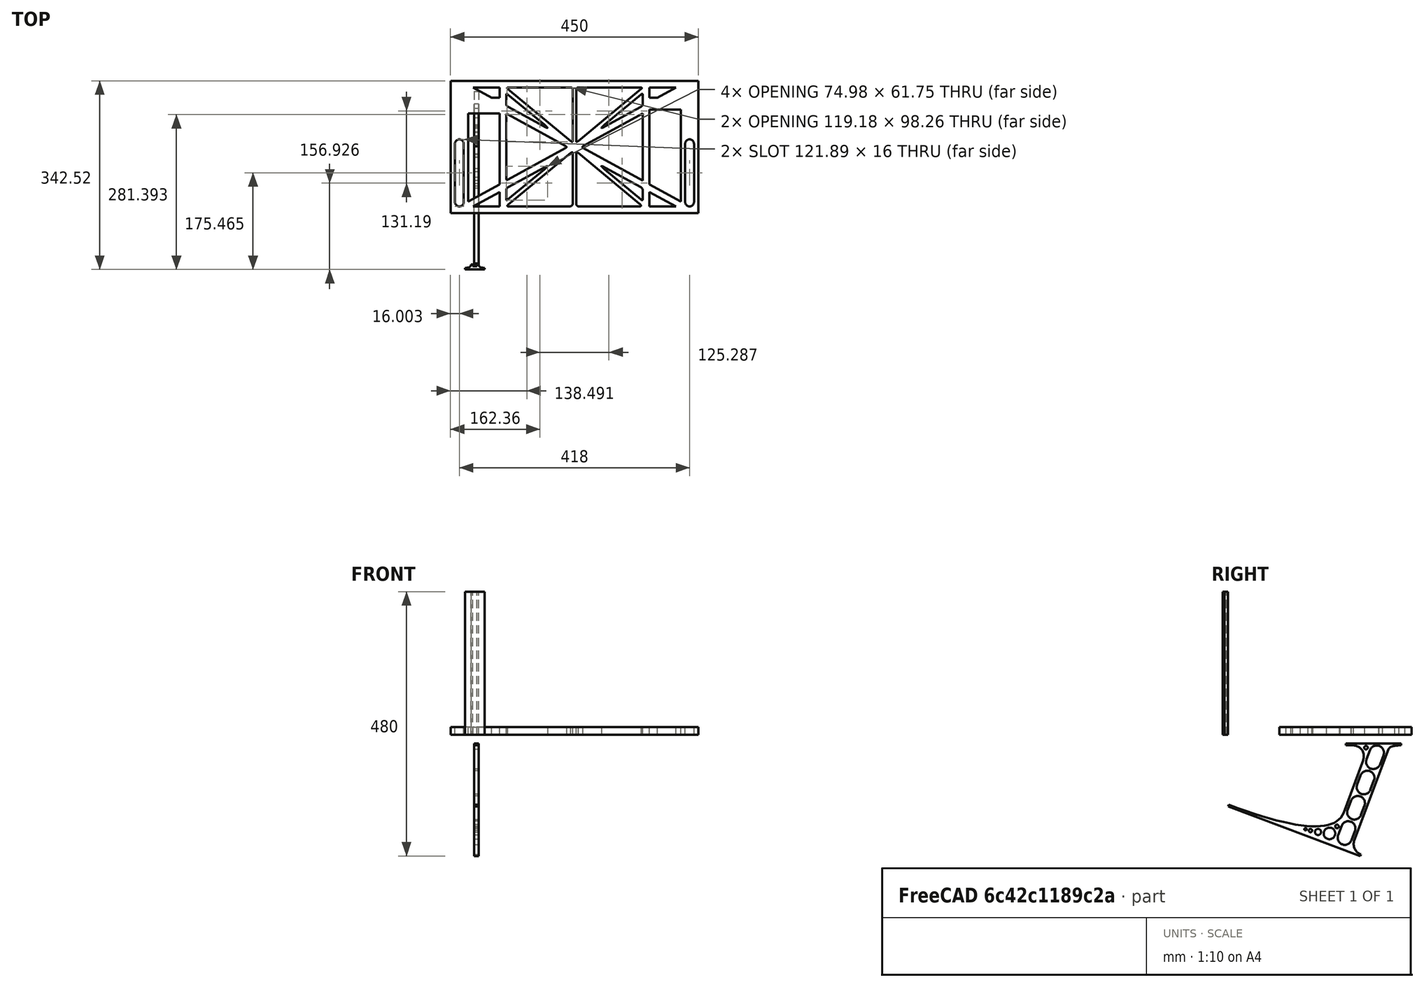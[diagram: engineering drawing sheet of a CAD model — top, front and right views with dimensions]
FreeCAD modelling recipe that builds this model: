
FCSTD DOCUMENT  (FreeCAD 0.19R0.19.2)
Label: laptopStand088
License: All rights reserved
LicenseURL: http://en.wikipedia.org/wiki/All_rights_reserved
objects: Sketcher::SketchObject×3, Part::Extrusion×3
note: 6 computed .brp shape members not serialized (recipe doc carries the construction recipe); baked Part::Feature solids carry a one-line shape summary decoded from their .brp

FEATURE [Sketcher::SketchObject] Sketch
  FullyConstrained = true
  sketch-geometry (232):
    g0: LineSegment StartX=-10.9272 StartY=-82.7794 StartZ=0 EndX=46.0728 EndY=-51.4823 EndZ=0
    g1: LineSegment StartX=366.073 StartY=-91.7794 StartZ=0 EndX=318.073 EndY=-65.424 EndZ=0
    g2: LineSegment StartX=-10.9272 StartY=77.3346 StartZ=0 EndX=-10.9272 EndY=-82.7794 EndZ=0
    g3: LineSegment StartX=375.073 StartY=-82.7794 StartZ=0 EndX=375.073 EndY=83.9235 EndZ=0
    g4: LineSegment StartX=-1.92719 StartY=-91.7794 StartZ=0 EndX=46.0728 EndY=-91.7794 EndZ=0
    g5: LineSegment StartX=318.073 StartY=124.221 StartZ=0 EndX=366.073 EndY=124.221 EndZ=0
    g6: LineSegment StartX=306.073 StartY=77.3346 StartZ=0 EndX=306.073 EndY=-44.8935 EndZ=0
    g7: LineSegment StartX=318.073 StartY=83.9235 StartZ=0 EndX=318.073 EndY=-51.4823 EndZ=0
    g8: LineSegment StartX=318.073 StartY=-51.4823 StartZ=0 EndX=375.073 EndY=-82.7794 EndZ=0
    g9: LineSegment StartX=318.073 StartY=-65.424 StartZ=0 EndX=318.073 EndY=-91.7794 EndZ=0
    g10: LineSegment StartX=318.073 StartY=-91.7794 StartZ=0 EndX=366.073 EndY=-91.7794 EndZ=0
    g11: LineSegment StartX=46.0728 StartY=-65.424 StartZ=0 EndX=-1.92719 EndY=-91.7794 EndZ=0
    g12: LineSegment StartX=46.0728 StartY=-65.424 StartZ=0 EndX=46.0728 EndY=-91.7794 EndZ=0
    g13: LineSegment StartX=46.0728 StartY=77.3346 StartZ=0 EndX=46.0728 EndY=-51.4823 EndZ=0
    g14: LineSegment StartX=-42.9272 StartY=136.221 StartZ=0 EndX=-42.9272 EndY=-103.779 EndZ=0
    g15: LineSegment StartX=407.073 StartY=136.221 StartZ=0 EndX=407.073 EndY=-103.779 EndZ=0
    g16: ArcOfCircle CenterX=-26.9272 CenterY=22.1087 CenterZ=0 NormalX=0 NormalY=0 NormalZ=1 AngleXU=0 Radius=8 StartAngle=1e-16 EndAngle=3.14159
    g17: ArcOfCircle CenterX=-26.9272 CenterY=-83.7794 CenterZ=0 NormalX=0 NormalY=0 NormalZ=1 AngleXU=0 Radius=8 StartAngle=3.14159 EndAngle=6.28319
    g18: LineSegment StartX=-34.9272 StartY=22.1087 StartZ=0 EndX=-34.9272 EndY=-83.7794 EndZ=0
    g19: LineSegment StartX=-18.9272 StartY=22.1087 StartZ=0 EndX=-18.9272 EndY=-83.7794 EndZ=0
    g20: ArcOfCircle CenterX=391.073 CenterY=22.1087 CenterZ=0 NormalX=0 NormalY=0 NormalZ=1 AngleXU=0 Radius=8 StartAngle=-4.4e-15 EndAngle=3.14159
    g21: LineSegment StartX=399.073 StartY=22.1087 StartZ=0 EndX=399.073 EndY=-83.7794 EndZ=0
    g22: LineSegment StartX=383.073 StartY=22.1087 StartZ=0 EndX=383.073 EndY=-83.7794 EndZ=0
    g23: ArcOfCircle CenterX=391.073 CenterY=-83.7794 CenterZ=0 NormalX=0 NormalY=0 NormalZ=1 AngleXU=0 Radius=8 StartAngle=3.14159 EndAngle=6.28319
    g24: Circle CenterX=175.022 CenterY=27.0628 CenterZ=0 NormalX=0 NormalY=0 NormalZ=1 AngleXU=0 Radius=1
    g25: Circle CenterX=179.022 CenterY=24.8665 CenterZ=0 NormalX=0 NormalY=0 NormalZ=1 AngleXU=0 Radius=1
    g26: Circle CenterX=179.022 CenterY=27.0628 CenterZ=0 NormalX=0 NormalY=0 NormalZ=1 AngleXU=0 Radius=1
    g27: BSplineCurve PolesCount=3 KnotsCount=2 Degree=2 IsPeriodic=0
    g28: GeomPoint X=175.022 Y=27.0628 Z=0
    g29: GeomPoint X=179.022 Y=27.0628 Z=0
    g30: Circle CenterX=189.124 CenterY=27.0628 CenterZ=0 NormalX=0 NormalY=0 NormalZ=1 AngleXU=0 Radius=1
    g31: Circle CenterX=185.124 CenterY=24.8665 CenterZ=0 NormalX=0 NormalY=0 NormalZ=1 AngleXU=0 Radius=1
    g32: Circle CenterX=185.124 CenterY=27.0628 CenterZ=0 NormalX=0 NormalY=0 NormalZ=1 AngleXU=0 Radius=1
    g33: BSplineCurve PolesCount=3 KnotsCount=2 Degree=2 IsPeriodic=0
    g34: GeomPoint X=189.124 Y=27.0628 Z=0
    g35: GeomPoint X=185.124 Y=27.0628 Z=0
    g36: Circle CenterX=175.022 CenterY=5.37834 CenterZ=0 NormalX=0 NormalY=0 NormalZ=1 AngleXU=0 Radius=1
    g37: Circle CenterX=179.022 CenterY=7.57463 CenterZ=0 NormalX=0 NormalY=0 NormalZ=1 AngleXU=0 Radius=1
    g38: Circle CenterX=179.022 CenterY=5.34704 CenterZ=0 NormalX=0 NormalY=0 NormalZ=1 AngleXU=0 Radius=1
    g39: BSplineCurve PolesCount=3 KnotsCount=2 Degree=2 IsPeriodic=0
    g40: GeomPoint X=175.022 Y=5.37834 Z=0
    g41: GeomPoint X=179.022 Y=5.34704 Z=0
    g42: Circle CenterX=189.124 CenterY=5.37834 CenterZ=0 NormalX=0 NormalY=0 NormalZ=1 AngleXU=0 Radius=1
    g43: Circle CenterX=185.124 CenterY=7.57463 CenterZ=0 NormalX=0 NormalY=0 NormalZ=1 AngleXU=0 Radius=1
    g44: Circle CenterX=185.124 CenterY=5.34704 CenterZ=0 NormalX=0 NormalY=0 NormalZ=1 AngleXU=0 Radius=1
    g45: BSplineCurve PolesCount=3 KnotsCount=2 Degree=2 IsPeriodic=0
    g46: GeomPoint X=189.124 Y=5.37834 Z=0
    g47: GeomPoint X=185.124 Y=5.34704 Z=0
    g48: Circle CenterX=165.871 CenterY=18.1458 CenterZ=0 NormalX=0 NormalY=0 NormalZ=1 AngleXU=0 Radius=1
    g49: Circle CenterX=169.377 CenterY=16.2206 CenterZ=0 NormalX=0 NormalY=0 NormalZ=1 AngleXU=0 Radius=1
    g50: Circle CenterX=165.871 CenterY=14.2954 CenterZ=0 NormalX=0 NormalY=0 NormalZ=1 AngleXU=0 Radius=1
    g51: BSplineCurve PolesCount=3 KnotsCount=2 Degree=2 IsPeriodic=0
    g52: GeomPoint X=165.871 Y=18.1458 Z=0
    g53: GeomPoint X=165.871 Y=14.2954 Z=0
    g54: Circle CenterX=198.275 CenterY=18.1458 CenterZ=0 NormalX=0 NormalY=0 NormalZ=1 AngleXU=0 Radius=1
    g55: Circle CenterX=194.768 CenterY=16.2206 CenterZ=0 NormalX=0 NormalY=0 NormalZ=1 AngleXU=0 Radius=1
    g56: Circle CenterX=198.275 CenterY=14.2954 CenterZ=0 NormalX=0 NormalY=0 NormalZ=1 AngleXU=0 Radius=1
    g57: BSplineCurve PolesCount=3 KnotsCount=2 Degree=2 IsPeriodic=0
    g58: GeomPoint X=198.275 Y=18.1458 Z=0
    g59: GeomPoint X=198.275 Y=14.2954 Z=0
    g60: LineSegment StartX=198.275 StartY=18.1458 StartZ=0 EndX=306.073 EndY=77.3346 EndZ=0
    g61: LineSegment StartX=198.275 StartY=14.2954 StartZ=0 EndX=306.073 EndY=-44.8935 EndZ=0
    g62: LineSegment StartX=407.073 StartY=-103.779 StartZ=0 EndX=-42.9272 EndY=-103.779 EndZ=0
    g63: LineSegment StartX=407.073 StartY=136.221 StartZ=0 EndX=-42.9272 EndY=136.221 EndZ=0
    g64: LineSegment StartX=46.0728 StartY=77.3346 StartZ=0 EndX=-10.9272 EndY=77.3346 EndZ=0
    g65: LineSegment StartX=46.0728 StartY=105.865 StartZ=0 EndX=31.5028 EndY=105.865 EndZ=0
    g66: LineSegment StartX=46.0728 StartY=124.221 StartZ=0 EndX=46.0728 EndY=105.865 EndZ=0
    g67: LineSegment StartX=-1.92719 StartY=124.221 StartZ=0 EndX=31.5028 EndY=105.865 EndZ=0
    g68: LineSegment StartX=46.0728 StartY=124.221 StartZ=0 EndX=-1.92719 EndY=124.221 EndZ=0
    g69: LineSegment StartX=318.073 StartY=83.9235 StartZ=0 EndX=375.073 EndY=83.9235 EndZ=0
    g70: LineSegment StartX=318.073 StartY=105.865 StartZ=0 EndX=332.643 EndY=105.865 EndZ=0
    g71: LineSegment StartX=332.643 StartY=105.865 StartZ=0 EndX=366.073 EndY=124.221 EndZ=0
    g72: LineSegment StartX=318.073 StartY=124.221 StartZ=0 EndX=318.073 EndY=105.865 EndZ=0
    g73: Circle CenterX=125.607 CenterY=54.1951 CenterZ=0 NormalX=0 NormalY=0 NormalZ=1 AngleXU=0 Radius=1
    g74: Circle CenterX=139.632 CenterY=46.4944 CenterZ=0 NormalX=0 NormalY=0 NormalZ=1 AngleXU=0 Radius=1
    g75: Circle CenterX=127.326 CenterY=56.7187 CenterZ=0 NormalX=0 NormalY=0 NormalZ=1 AngleXU=0 Radius=1
    g76: BSplineCurve PolesCount=3 KnotsCount=2 Degree=2 IsPeriodic=0
    g77: GeomPoint X=125.607 Y=54.1951 Z=0
    g78: GeomPoint X=127.326 Y=56.7187 Z=0
    g79: Circle CenterX=236.821 CenterY=56.7187 CenterZ=0 NormalX=0 NormalY=0 NormalZ=1 AngleXU=0 Radius=1
    g80: Circle CenterX=224.513 CenterY=46.4944 CenterZ=0 NormalX=0 NormalY=0 NormalZ=1 AngleXU=0 Radius=1
    g81: Circle CenterX=238.538 CenterY=54.1951 CenterZ=0 NormalX=0 NormalY=0 NormalZ=1 AngleXU=0 Radius=1
    g82: BSplineCurve PolesCount=3 KnotsCount=2 Degree=2 IsPeriodic=0
    g83: GeomPoint X=236.821 Y=56.7187 Z=0
    g84: GeomPoint X=238.538 Y=54.1951 Z=0
    g85: Circle CenterX=238.538 CenterY=-21.7539 CenterZ=0 NormalX=0 NormalY=0 NormalZ=1 AngleXU=0 Radius=1
    g86: Circle CenterX=224.513 CenterY=-14.0532 CenterZ=0 NormalX=0 NormalY=0 NormalZ=1 AngleXU=0 Radius=1
    g87: Circle CenterX=236.821 CenterY=-24.2775 CenterZ=0 NormalX=0 NormalY=0 NormalZ=1 AngleXU=0 Radius=1
    g88: BSplineCurve PolesCount=3 KnotsCount=2 Degree=2 IsPeriodic=0
    g89: GeomPoint X=238.538 Y=-21.7539 Z=0
    g90: GeomPoint X=236.821 Y=-24.2775 Z=0
    g91: Circle CenterX=125.607 CenterY=-21.7539 CenterZ=0 NormalX=0 NormalY=0 NormalZ=1 AngleXU=0 Radius=1
    g92: Circle CenterX=139.632 CenterY=-14.0532 CenterZ=0 NormalX=0 NormalY=0 NormalZ=1 AngleXU=0 Radius=1
    g93: Circle CenterX=127.325 CenterY=-24.2775 CenterZ=0 NormalX=0 NormalY=0 NormalZ=1 AngleXU=0 Radius=1
    g94: BSplineCurve PolesCount=3 KnotsCount=2 Degree=2 IsPeriodic=0
    g95: GeomPoint X=125.607 Y=-21.7539 Z=0
    g96: GeomPoint X=127.325 Y=-24.2775 Z=0
    g97: Circle CenterX=302.996 CenterY=111.695 CenterZ=0 NormalX=0 NormalY=0 NormalZ=1 AngleXU=0 Radius=1
    g98: Circle CenterX=306.073 CenterY=114.251 CenterZ=0 NormalX=0 NormalY=0 NormalZ=1 AngleXU=0 Radius=1
    g99: Circle CenterX=306.073 CenterY=110.251 CenterZ=0 NormalX=0 NormalY=0 NormalZ=1 AngleXU=0 Radius=1
    g100: BSplineCurve PolesCount=3 KnotsCount=2 Degree=2 IsPeriodic=0
    g101: GeomPoint X=302.996 Y=111.695 Z=0
    g102: GeomPoint X=306.073 Y=110.251 Z=0
    g103: Circle CenterX=306.073 CenterY=95.2763 CenterZ=0 NormalX=0 NormalY=0 NormalZ=1 AngleXU=0 Radius=1
    g104: Circle CenterX=306.073 CenterY=91.2763 CenterZ=0 NormalX=0 NormalY=0 NormalZ=1 AngleXU=0 Radius=1
    g105: Circle CenterX=302.567 CenterY=89.3511 CenterZ=0 NormalX=0 NormalY=0 NormalZ=1 AngleXU=0 Radius=1
    g106: BSplineCurve PolesCount=3 KnotsCount=2 Degree=2 IsPeriodic=0
    g107: GeomPoint X=306.073 Y=95.2763 Z=0
    g108: GeomPoint X=302.567 Y=89.3511 Z=0
    g109: LineSegment StartX=306.073 StartY=110.251 StartZ=0 EndX=306.073 EndY=95.2763 EndZ=0
    g110: LineSegment StartX=302.996 StartY=111.695 StartZ=0 EndX=236.821 EndY=56.7187 EndZ=0
    g111: LineSegment StartX=238.538 StartY=54.1951 StartZ=0 EndX=302.567 EndY=89.3511 EndZ=0
    g112: Circle CenterX=61.1496 CenterY=111.695 CenterZ=0 NormalX=0 NormalY=0 NormalZ=1 AngleXU=0 Radius=1
    g113: Circle CenterX=58.0728 CenterY=114.251 CenterZ=0 NormalX=0 NormalY=0 NormalZ=1 AngleXU=0 Radius=1
    g114: Circle CenterX=58.0728 CenterY=110.251 CenterZ=0 NormalX=0 NormalY=0 NormalZ=1 AngleXU=0 Radius=1
    g115: BSplineCurve PolesCount=3 KnotsCount=2 Degree=2 IsPeriodic=0
    g116: GeomPoint X=61.1496 Y=111.695 Z=0
    g117: GeomPoint X=58.0728 Y=110.251 Z=0
    g118: Circle CenterX=61.5791 CenterY=89.3511 CenterZ=0 NormalX=0 NormalY=0 NormalZ=1 AngleXU=0 Radius=1
    g119: Circle CenterX=58.0728 CenterY=91.2763 CenterZ=0 NormalX=0 NormalY=0 NormalZ=1 AngleXU=0 Radius=1
    g120: Circle CenterX=58.0728 CenterY=95.2763 CenterZ=0 NormalX=0 NormalY=0 NormalZ=1 AngleXU=0 Radius=1
    g121: BSplineCurve PolesCount=3 KnotsCount=2 Degree=2 IsPeriodic=0
    g122: GeomPoint X=61.5791 Y=89.3511 Z=0
    g123: GeomPoint X=58.0728 Y=95.2763 Z=0
    g124: LineSegment StartX=58.0728 StartY=110.251 StartZ=0 EndX=58.0728 EndY=95.2763 EndZ=0
    g125: LineSegment StartX=61.1496 StartY=111.695 StartZ=0 EndX=127.326 EndY=56.7187 EndZ=0
    g126: LineSegment StartX=125.607 StartY=54.1951 StartZ=0 EndX=61.5791 EndY=89.3511 EndZ=0
    g127: Circle CenterX=61.5791 CenterY=-56.9099 CenterZ=0 NormalX=0 NormalY=0 NormalZ=1 AngleXU=0 Radius=1
    g128: Circle CenterX=58.0728 CenterY=-58.8351 CenterZ=0 NormalX=0 NormalY=0 NormalZ=1 AngleXU=0 Radius=1
    g129: Circle CenterX=58.0728 CenterY=-62.8351 CenterZ=0 NormalX=0 NormalY=0 NormalZ=1 AngleXU=0 Radius=1
    g130: BSplineCurve PolesCount=3 KnotsCount=2 Degree=2 IsPeriodic=0
    g131: GeomPoint X=61.5791 Y=-56.9099 Z=0
    g132: GeomPoint X=58.0728 Y=-62.8351 Z=0
    g133: Circle CenterX=58.0728 CenterY=-77.8102 CenterZ=0 NormalX=0 NormalY=0 NormalZ=1 AngleXU=0 Radius=1
    g134: Circle CenterX=58.0728 CenterY=-81.8102 CenterZ=0 NormalX=0 NormalY=0 NormalZ=1 AngleXU=0 Radius=1
    g135: Circle CenterX=61.1496 CenterY=-79.2541 CenterZ=0 NormalX=0 NormalY=0 NormalZ=1 AngleXU=0 Radius=1
    g136: BSplineCurve PolesCount=3 KnotsCount=2 Degree=2 IsPeriodic=0
    g137: GeomPoint X=58.0728 Y=-77.8102 Z=0
    g138: GeomPoint X=61.1496 Y=-79.2541 Z=0
    g139: LineSegment StartX=58.0728 StartY=-62.8351 StartZ=0 EndX=58.0728 EndY=-77.8102 EndZ=0
    g140: LineSegment StartX=61.1496 StartY=-79.2541 StartZ=0 EndX=127.325 EndY=-24.2775 EndZ=0
    g141: LineSegment StartX=125.607 StartY=-21.7539 StartZ=0 EndX=61.5791 EndY=-56.9099 EndZ=0
    g142: Circle CenterX=302.567 CenterY=-56.9099 CenterZ=0 NormalX=0 NormalY=0 NormalZ=1 AngleXU=0 Radius=1
    g143: Circle CenterX=306.073 CenterY=-58.8351 CenterZ=0 NormalX=0 NormalY=0 NormalZ=1 AngleXU=0 Radius=1
    g144: Circle CenterX=306.073 CenterY=-62.8351 CenterZ=0 NormalX=0 NormalY=0 NormalZ=1 AngleXU=0 Radius=1
    g145: BSplineCurve PolesCount=3 KnotsCount=2 Degree=2 IsPeriodic=0
    g146: GeomPoint X=302.567 Y=-56.9099 Z=0
    g147: GeomPoint X=306.073 Y=-62.8351 Z=0
    g148: Circle CenterX=302.996 CenterY=-79.2541 CenterZ=0 NormalX=0 NormalY=0 NormalZ=1 AngleXU=0 Radius=1
    g149: Circle CenterX=306.073 CenterY=-81.8102 CenterZ=0 NormalX=0 NormalY=0 NormalZ=1 AngleXU=0 Radius=1
    g150: Circle CenterX=306.073 CenterY=-77.8102 CenterZ=0 NormalX=0 NormalY=0 NormalZ=1 AngleXU=0 Radius=1
    g151: BSplineCurve PolesCount=3 KnotsCount=2 Degree=2 IsPeriodic=0
    g152: GeomPoint X=302.996 Y=-79.2541 Z=0
    g153: GeomPoint X=306.073 Y=-77.8102 Z=0
    g154: LineSegment StartX=306.073 StartY=-62.8351 StartZ=0 EndX=306.073 EndY=-77.8102 EndZ=0
    g155: LineSegment StartX=302.996 StartY=-79.2541 StartZ=0 EndX=236.821 EndY=-24.2775 EndZ=0
    g156: LineSegment StartX=238.538 StartY=-21.7539 StartZ=0 EndX=302.567 EndY=-56.9099 EndZ=0
    g157: Circle CenterX=61.6457 CenterY=-88.8112 CenterZ=0 NormalX=0 NormalY=0 NormalZ=1 AngleXU=0 Radius=1
    g158: Circle CenterX=58.0728 CenterY=-91.7794 CenterZ=0 NormalX=0 NormalY=0 NormalZ=1 AngleXU=0 Radius=1
    g159: Circle CenterX=63.9135 CenterY=-91.7794 CenterZ=0 NormalX=0 NormalY=0 NormalZ=1 AngleXU=0 Radius=1
    g160: BSplineCurve PolesCount=3 KnotsCount=2 Degree=2 IsPeriodic=0
    g161: GeomPoint X=61.6457 Y=-88.8112 Z=0
    g162: GeomPoint X=63.9135 Y=-91.7794 Z=0
    g163: Circle CenterX=179.022 CenterY=-85.8163 CenterZ=0 NormalX=0 NormalY=0 NormalZ=1 AngleXU=0 Radius=1
    g164: Circle CenterX=179.022 CenterY=-91.7794 CenterZ=0 NormalX=0 NormalY=0 NormalZ=1 AngleXU=0 Radius=1
    g165: Circle CenterX=171.895 CenterY=-91.7794 CenterZ=0 NormalX=0 NormalY=0 NormalZ=1 AngleXU=0 Radius=1
    g166: BSplineCurve PolesCount=3 KnotsCount=2 Degree=2 IsPeriodic=0
    g167: GeomPoint X=179.022 Y=-85.8163 Z=0
    g168: GeomPoint X=171.895 Y=-91.7794 Z=0
    g169: Circle CenterX=185.124 CenterY=-86.2028 CenterZ=0 NormalX=0 NormalY=0 NormalZ=1 AngleXU=0 Radius=1
    g170: Circle CenterX=185.124 CenterY=-91.7794 CenterZ=0 NormalX=0 NormalY=0 NormalZ=1 AngleXU=0 Radius=1
    g171: Circle CenterX=191.747 CenterY=-91.7794 CenterZ=0 NormalX=0 NormalY=0 NormalZ=1 AngleXU=0 Radius=1
    g172: BSplineCurve PolesCount=3 KnotsCount=2 Degree=2 IsPeriodic=0
    g173: GeomPoint X=185.124 Y=-86.2028 Z=0
    g174: GeomPoint X=191.747 Y=-91.7794 Z=0
    g175: Circle CenterX=299.888 CenterY=-86.6413 CenterZ=0 NormalX=0 NormalY=0 NormalZ=1 AngleXU=0 Radius=1
    g176: Circle CenterX=306.073 CenterY=-91.7794 CenterZ=0 NormalX=0 NormalY=0 NormalZ=1 AngleXU=0 Radius=1
    g177: Circle CenterX=298.776 CenterY=-91.7794 CenterZ=0 NormalX=0 NormalY=0 NormalZ=1 AngleXU=0 Radius=1
    g178: BSplineCurve PolesCount=3 KnotsCount=2 Degree=2 IsPeriodic=0
    g179: GeomPoint X=299.888 Y=-86.6413 Z=0
    g180: GeomPoint X=298.776 Y=-91.7794 Z=0
    g181: LineSegment StartX=189.124 StartY=5.37834 StartZ=0 EndX=299.888 EndY=-86.6413 EndZ=0
    g182: LineSegment StartX=298.776 StartY=-91.7794 StartZ=0 EndX=191.747 EndY=-91.7794 EndZ=0
    g183: LineSegment StartX=185.124 StartY=-86.2028 StartZ=0 EndX=185.124 EndY=5.34704 EndZ=0
    g184: LineSegment StartX=179.022 StartY=5.34704 StartZ=0 EndX=179.022 EndY=-85.8163 EndZ=0
    g185: LineSegment StartX=171.895 StartY=-91.7794 StartZ=0 EndX=63.9135 EndY=-91.7794 EndZ=0
    g186: LineSegment StartX=61.6457 StartY=-88.8112 StartZ=0 EndX=175.022 EndY=5.37834 EndZ=0
    g187: Circle CenterX=302.073 CenterY=124.221 CenterZ=0 NormalX=0 NormalY=0 NormalZ=1 AngleXU=0 Radius=1
    g188: Circle CenterX=306.073 CenterY=124.221 CenterZ=0 NormalX=0 NormalY=0 NormalZ=1 AngleXU=0 Radius=1
    g189: Circle CenterX=302.996 CenterY=121.665 CenterZ=0 NormalX=0 NormalY=0 NormalZ=1 AngleXU=0 Radius=1
    g190: BSplineCurve PolesCount=3 KnotsCount=2 Degree=2 IsPeriodic=0
    g191: GeomPoint X=302.073 Y=124.221 Z=0
    g192: GeomPoint X=302.996 Y=121.665 Z=0
    g193: Circle CenterX=189.124 CenterY=124.221 CenterZ=0 NormalX=0 NormalY=0 NormalZ=1 AngleXU=0 Radius=1
    g194: Circle CenterX=185.124 CenterY=124.221 CenterZ=0 NormalX=0 NormalY=0 NormalZ=1 AngleXU=0 Radius=1
    g195: Circle CenterX=185.124 CenterY=120.221 CenterZ=0 NormalX=0 NormalY=0 NormalZ=1 AngleXU=0 Radius=1
    g196: BSplineCurve PolesCount=3 KnotsCount=2 Degree=2 IsPeriodic=0
    g197: GeomPoint X=189.124 Y=124.221 Z=0
    g198: GeomPoint X=185.124 Y=120.221 Z=0
    g199: Circle CenterX=175.022 CenterY=124.221 CenterZ=0 NormalX=0 NormalY=0 NormalZ=1 AngleXU=0 Radius=1
    g200: Circle CenterX=179.022 CenterY=124.221 CenterZ=0 NormalX=0 NormalY=0 NormalZ=1 AngleXU=0 Radius=1
    g201: Circle CenterX=179.022 CenterY=120.221 CenterZ=0 NormalX=0 NormalY=0 NormalZ=1 AngleXU=0 Radius=1
    g202: BSplineCurve PolesCount=3 KnotsCount=2 Degree=2 IsPeriodic=0
    g203: GeomPoint X=175.022 Y=124.221 Z=0
    g204: GeomPoint X=179.022 Y=120.221 Z=0
    g205: Circle CenterX=62.0728 CenterY=124.221 CenterZ=0 NormalX=0 NormalY=0 NormalZ=1 AngleXU=0 Radius=1
    g206: Circle CenterX=58.0728 CenterY=124.221 CenterZ=0 NormalX=0 NormalY=0 NormalZ=1 AngleXU=0 Radius=1
    g207: Circle CenterX=61.1496 CenterY=121.665 CenterZ=0 NormalX=0 NormalY=0 NormalZ=1 AngleXU=0 Radius=1
    g208: BSplineCurve PolesCount=3 KnotsCount=2 Degree=2 IsPeriodic=0
    g209: GeomPoint X=62.0728 Y=124.221 Z=0
    g210: GeomPoint X=61.1496 Y=121.665 Z=0
    g211: LineSegment StartX=62.0728 StartY=124.221 StartZ=0 EndX=175.022 EndY=124.221 EndZ=0
    g212: LineSegment StartX=179.022 StartY=120.221 StartZ=0 EndX=179.022 EndY=27.0628 EndZ=0
    g213: LineSegment StartX=185.124 StartY=27.0628 StartZ=0 EndX=185.124 EndY=120.221 EndZ=0
    g214: LineSegment StartX=189.124 StartY=124.221 StartZ=0 EndX=302.073 EndY=124.221 EndZ=0
    g215: LineSegment StartX=302.996 StartY=121.665 StartZ=0 EndX=189.124 EndY=27.0628 EndZ=0
    g216: LineSegment StartX=175.022 StartY=27.0628 StartZ=0 EndX=61.1496 EndY=121.665 EndZ=0
    g217: Circle CenterX=61.5791 CenterY=75.4095 CenterZ=0 NormalX=0 NormalY=0 NormalZ=1 AngleXU=0 Radius=1
    g218: Circle CenterX=58.0728 CenterY=77.3346 CenterZ=0 NormalX=0 NormalY=0 NormalZ=1 AngleXU=0 Radius=1
    g219: Circle CenterX=58.0728 CenterY=73.3346 CenterZ=0 NormalX=0 NormalY=0 NormalZ=1 AngleXU=0 Radius=1
    g220: BSplineCurve PolesCount=3 KnotsCount=2 Degree=2 IsPeriodic=0
    g221: GeomPoint X=61.5791 Y=75.4095 Z=0
    g222: GeomPoint X=58.0728 Y=73.3346 Z=0
    g223: Circle CenterX=58.0728 CenterY=-40.8935 CenterZ=0 NormalX=0 NormalY=0 NormalZ=1 AngleXU=0 Radius=1
    g224: Circle CenterX=58.0728 CenterY=-44.8935 CenterZ=0 NormalX=0 NormalY=0 NormalZ=1 AngleXU=0 Radius=1
    g225: Circle CenterX=61.5791 CenterY=-42.9683 CenterZ=0 NormalX=0 NormalY=0 NormalZ=1 AngleXU=0 Radius=1
    g226: BSplineCurve PolesCount=3 KnotsCount=2 Degree=2 IsPeriodic=0
    g227: GeomPoint X=58.0728 Y=-40.8935 Z=0
    g228: GeomPoint X=61.5791 Y=-42.9683 Z=0
    g229: LineSegment StartX=61.5791 StartY=-42.9683 StartZ=0 EndX=165.871 EndY=14.2954 EndZ=0
    g230: LineSegment StartX=165.871 StartY=18.1458 StartZ=0 EndX=61.5791 EndY=75.4095 EndZ=0
    g231: LineSegment StartX=58.0728 StartY=73.3346 StartZ=0 EndX=58.0728 EndY=-40.8935 EndZ=0
  constraints (395):
    c: Horizontal(g4)
    c: Horizontal(g5)
    c: Coincident(g7,g8)
    c: Coincident(g9,g1)
    c: Tangent(g7,g9)
    c: Coincident(g12,g11)
    c: Coincident(g0,g13)
    c: Block(g8)
    c: Block(g3)
    c: Block(g1)
    c: Block(g9)
    c: Block(g12)
    c: Block(g11)
    c: Block(g0)
    c: Block(g2)
    c: Block(g6)
    c: Block(g5)
    c: Block(g10)
    c: Block(g4)
    c: Vertical(g14)
    c: Vertical(g15)
    c: Block(g15)
    c: Block(g14)
    c: Tangent(g16,g19) = 1.5708
    c: Tangent(g16,g18) = -1.5708
    c: Tangent(g18,g17) = -1.5708
    c: Tangent(g19,g17) = 1.5708
    c: Vertical(g18)
    c: Equal(g16,g17)
    c: Block(g19)
    c: Block(g18)
    c: Tangent(g20,g21) = 1.5708
    c: Tangent(g21,g23) = 1.5708
    c: Equal(g20,g23)
    c: Coincident(g22,g20)
    c: Coincident(g22,g23)
    c: Block(g21)
    c: Block(g22)
    c: Weight(g24) = 1
    c: Equal(g24,g25)
    c: Equal(g24,g26)
    c: InternalAlignment(g24,g27)
    c: InternalAlignment(g25,g27)
    c: InternalAlignment(g26,g27)
    c: InternalAlignment(g28,g27)
    c: InternalAlignment(g29,g27)
    c: Weight(g30) = 1
    c: Equal(g30,g31)
    c: Equal(g30,g32)
    c: InternalAlignment(g30,g33)
    c: InternalAlignment(g31,g33)
    c: InternalAlignment(g32,g33)
    c: InternalAlignment(g34,g33)
    c: InternalAlignment(g35,g33)
    c: Block(g33)
    c: Block(g27)
    c: Weight(g36) = 1
    c: Equal(g36,g37)
    c: Equal(g36,g38)
    c: InternalAlignment(g36,g39)
    c: InternalAlignment(g37,g39)
    c: InternalAlignment(g38,g39)
    c: InternalAlignment(g40,g39)
    c: InternalAlignment(g41,g39)
    c: Weight(g42) = 1
    c: Equal(g42,g43)
    c: Equal(g42,g44)
    c: InternalAlignment(g42,g45)
    c: InternalAlignment(g43,g45)
    c: InternalAlignment(g44,g45)
    c: InternalAlignment(g46,g45)
    c: InternalAlignment(g47,g45)
    c: Block(g45)
    c: Block(g39)
    c: Weight(g48) = 1
    c: Equal(g48,g49)
    c: Equal(g48,g50)
    c: InternalAlignment(g48,g51)
    c: InternalAlignment(g49,g51)
    c: InternalAlignment(g50,g51)
    c: InternalAlignment(g52,g51)
    c: InternalAlignment(g53,g51)
    c: Weight(g54) = 1
    c: Equal(g54,g55)
    c: Equal(g54,g56)
    c: InternalAlignment(g54,g57)
    c: InternalAlignment(g55,g57)
    c: InternalAlignment(g56,g57)
    c: InternalAlignment(g58,g57)
    c: InternalAlignment(g59,g57)
    c: Block(g51)
    c: Block(g57)
    c: Coincident(g60,g57)
    c: Coincident(g60,g6)
    c: Coincident(g61,g57)
    c: Coincident(g61,g6)
    c: Coincident(g62,g15)
    c: Coincident(g62,g14)
    c: Horizontal(g62)
    c: Distance(g62) = 450
    c: Coincident(g63,g15)
    c: Coincident(g63,g14)
    c: Horizontal(g63)
    c: Horizontal(g64)
    c: Coincident(g13,g64)
    c: Horizontal(g65)
    c: Vertical(g66)
    c: Block(g66)
    c: Block(g65)
    c: Block(g64)
    c: Distance(g66) = 18.3554
    c: Coincident(g68,g66)
    c: Coincident(g68,g67)
    c: Horizontal(g68)
    c: Block(g68)
    c: Block(g67)
    c: Coincident(g65,g67)
    c: Coincident(g2,g64)
    c: Coincident(g69,g7)
    c: Horizontal(g69)
    c: Horizontal(g70)
    c: Block(g69)
    c: Coincident(g71,g5)
    c: Coincident(g72,g5)
    c: Coincident(g72,g70)
    c: Vertical(g72)
    c: Block(g72)
    c: Coincident(g70,g71)
    c: Block(g71)
    c: Coincident(g3,g69)
    c: Weight(g73) = 1
    c: Equal(g73,g74)
    c: Equal(g73,g75)
    c: InternalAlignment(g73,g76)
    c: InternalAlignment(g74,g76)
    c: InternalAlignment(g75,g76)
    c: InternalAlignment(g77,g76)
    c: InternalAlignment(g78,g76)
    c: Block(g76)
    c: Weight(g79) = 1
    c: Equal(g79,g80)
    c: Equal(g79,g81)
    c: InternalAlignment(g79,g82)
    c: InternalAlignment(g80,g82)
    c: InternalAlignment(g81,g82)
    c: InternalAlignment(g83,g82)
    c: InternalAlignment(g84,g82)
    c: Block(g82)
    c: Weight(g85) = 1
    c: Equal(g85,g86)
    c: Equal(g85,g87)
    c: InternalAlignment(g85,g88)
    c: InternalAlignment(g86,g88)
    c: InternalAlignment(g87,g88)
    c: InternalAlignment(g89,g88)
    c: InternalAlignment(g90,g88)
    c: Block(g88)
    c: Weight(g91) = 1
    c: Equal(g91,g92)
    c: Equal(g91,g93)
    c: InternalAlignment(g91,g94)
    c: InternalAlignment(g92,g94)
    c: InternalAlignment(g93,g94)
    c: InternalAlignment(g95,g94)
    c: InternalAlignment(g96,g94)
    c: Block(g94)
    c: Weight(g97) = 1
    c: Equal(g97,g98)
    c: Equal(g97,g99)
    c: InternalAlignment(g97,g100)
    c: InternalAlignment(g98,g100)
    c: InternalAlignment(g99,g100)
    c: InternalAlignment(g101,g100)
    c: InternalAlignment(g102,g100)
    c: Weight(g103) = 1
    c: Equal(g103,g104)
    c: Equal(g103,g105)
    c: InternalAlignment(g103,g106)
    c: InternalAlignment(g104,g106)
    c: InternalAlignment(g105,g106)
    c: InternalAlignment(g107,g106)
    c: InternalAlignment(g108,g106)
    c: Block(g100)
    c: Block(g106)
    c: Coincident(g109,g100)
    c: Coincident(g109,g106)
    c: Vertical(g109)
    c: Coincident(g110,g100)
    c: Coincident(g110,g82)
    c: Coincident(g111,g82)
    c: Coincident(g111,g106)
    c: Weight(g112) = 1
    c: Equal(g112,g113)
    c: Equal(g112,g114)
    c: InternalAlignment(g112,g115)
    c: InternalAlignment(g113,g115)
    c: InternalAlignment(g114,g115)
    c: InternalAlignment(g116,g115)
    c: InternalAlignment(g117,g115)
    c: Weight(g118) = 1
    c: Equal(g118,g119)
    c: Equal(g118,g120)
    c: InternalAlignment(g118,g121)
    c: InternalAlignment(g119,g121)
    c: InternalAlignment(g120,g121)
    c: InternalAlignment(g122,g121)
    c: InternalAlignment(g123,g121)
    c: Block(g115)
    c: Block(g121)
    c: Coincident(g124,g115)
    c: Coincident(g124,g121)
    c: Vertical(g124)
    c: Coincident(g125,g115)
    c: Coincident(g125,g76)
    c: Coincident(g126,g76)
    c: Coincident(g126,g121)
    c: Weight(g127) = 1
    c: Equal(g127,g128)
    c: Equal(g127,g129)
    c: InternalAlignment(g127,g130)
    c: InternalAlignment(g128,g130)
    c: InternalAlignment(g129,g130)
    c: InternalAlignment(g131,g130)
    c: InternalAlignment(g132,g130)
    c: Weight(g133) = 1
    c: Equal(g133,g134)
    c: Equal(g133,g135)
    c: InternalAlignment(g133,g136)
    c: InternalAlignment(g134,g136)
    c: InternalAlignment(g135,g136)
    c: InternalAlignment(g137,g136)
    c: InternalAlignment(g138,g136)
    c: Block(g130)
    c: Block(g136)
    c: Coincident(g139,g130)
    c: Coincident(g139,g136)
    c: Vertical(g139)
    c: Coincident(g140,g136)
    c: Coincident(g140,g94)
    c: Coincident(g141,g94)
    c: Coincident(g141,g130)
    c: Weight(g142) = 1
    c: Equal(g142,g143)
    c: Equal(g142,g144)
    c: InternalAlignment(g142,g145)
    c: InternalAlignment(g143,g145)
    c: InternalAlignment(g144,g145)
    c: InternalAlignment(g146,g145)
    c: InternalAlignment(g147,g145)
    c: Weight(g148) = 1
    c: Equal(g148,g149)
    c: Equal(g148,g150)
    c: InternalAlignment(g148,g151)
    c: InternalAlignment(g149,g151)
    c: InternalAlignment(g150,g151)
    c: InternalAlignment(g152,g151)
    c: InternalAlignment(g153,g151)
    c: Block(g145)
    c: Block(g151)
    c: Coincident(g154,g145)
    c: Coincident(g154,g151)
    c: Vertical(g154)
    c: Coincident(g155,g151)
    c: Coincident(g155,g88)
    c: Coincident(g156,g88)
    c: Coincident(g156,g145)
    c: Weight(g157) = 1
    c: Equal(g157,g158)
    c: Equal(g157,g159)
    c: InternalAlignment(g157,g160)
    c: InternalAlignment(g158,g160)
    c: InternalAlignment(g159,g160)
    c: InternalAlignment(g161,g160)
    c: InternalAlignment(g162,g160)
    c: Weight(g163) = 1
    c: Equal(g163,g164)
    c: Equal(g163,g165)
    c: InternalAlignment(g163,g166)
    c: InternalAlignment(g164,g166)
    c: InternalAlignment(g165,g166)
    c: InternalAlignment(g167,g166)
    c: InternalAlignment(g168,g166)
    c: Weight(g169) = 1
    c: Equal(g169,g170)
    c: Equal(g169,g171)
    c: InternalAlignment(g169,g172)
    c: InternalAlignment(g170,g172)
    c: InternalAlignment(g171,g172)
    c: InternalAlignment(g173,g172)
    c: InternalAlignment(g174,g172)
    c: Weight(g175) = 1
    c: Equal(g175,g176)
    c: Equal(g175,g177)
    c: InternalAlignment(g175,g178)
    c: InternalAlignment(g176,g178)
    c: InternalAlignment(g177,g178)
    c: InternalAlignment(g179,g178)
    c: InternalAlignment(g180,g178)
    c: Block(g178)
    c: Block(g172)
    c: Block(g166)
    c: Block(g160)
    c: Coincident(g181,g45)
    c: Coincident(g181,g178)
    c: Coincident(g182,g178)
    c: Coincident(g182,g172)
    c: Horizontal(g182)
    c: Coincident(g183,g172)
    c: Coincident(g183,g45)
    c: Vertical(g183)
    c: Coincident(g184,g39)
    c: Coincident(g184,g166)
    c: Vertical(g184)
    c: Coincident(g185,g166)
    c: Coincident(g185,g160)
    c: Horizontal(g185)
    c: Coincident(g186,g160)
    c: Coincident(g186,g39)
    c: Weight(g187) = 1
    c: Equal(g187,g188)
    c: Equal(g187,g189)
    c: InternalAlignment(g187,g190)
    c: InternalAlignment(g188,g190)
    c: InternalAlignment(g189,g190)
    c: InternalAlignment(g191,g190)
    c: InternalAlignment(g192,g190)
    c: Weight(g193) = 1
    c: Equal(g193,g194)
    c: Equal(g193,g195)
    c: InternalAlignment(g193,g196)
    c: InternalAlignment(g194,g196)
    c: InternalAlignment(g195,g196)
    c: InternalAlignment(g197,g196)
    c: InternalAlignment(g198,g196)
    c: Weight(g199) = 1
    c: Equal(g199,g200)
    c: Equal(g199,g201)
    c: InternalAlignment(g199,g202)
    c: InternalAlignment(g200,g202)
    c: InternalAlignment(g201,g202)
    c: InternalAlignment(g203,g202)
    c: InternalAlignment(g204,g202)
    c: Weight(g205) = 1
    c: Equal(g205,g206)
    c: Equal(g205,g207)
    c: InternalAlignment(g205,g208)
    c: InternalAlignment(g206,g208)
    c: InternalAlignment(g207,g208)
    c: InternalAlignment(g209,g208)
    c: InternalAlignment(g210,g208)
    c: Block(g208)
    c: Block(g202)
    c: Block(g196)
    c: Block(g190)
    c: Coincident(g211,g208)
    c: Coincident(g211,g202)
    c: Horizontal(g211)
    c: Coincident(g212,g202)
    c: Coincident(g212,g27)
    c: Vertical(g212)
    c: Coincident(g213,g33)
    c: Coincident(g213,g196)
    c: Vertical(g213)
    c: Coincident(g214,g196)
    c: Coincident(g214,g190)
    c: Horizontal(g214)
    c: Coincident(g215,g190)
    c: Coincident(g215,g33)
    c: Coincident(g216,g27)
    c: Coincident(g216,g208)
    c: Weight(g217) = 1
    c: Equal(g217,g218)
    c: Equal(g217,g219)
    c: InternalAlignment(g217,g220)
    c: InternalAlignment(g218,g220)
    c: InternalAlignment(g219,g220)
    c: InternalAlignment(g221,g220)
    c: InternalAlignment(g222,g220)
    c: Weight(g223) = 1
    c: Equal(g223,g224)
    c: Equal(g223,g225)
    c: InternalAlignment(g223,g226)
    c: InternalAlignment(g224,g226)
    c: InternalAlignment(g225,g226)
    c: InternalAlignment(g227,g226)
    c: InternalAlignment(g228,g226)
    c: Block(g226)
    c: Block(g220)
    c: Coincident(g229,g226)
    c: Coincident(g229,g51)
    c: Coincident(g230,g51)
    c: Coincident(g230,g220)
    c: Coincident(g231,g220)
    c: Coincident(g231,g226)
    c: Vertical(g231)
FEATURE [Sketcher::SketchObject] Sketch001
  FullyConstrained = true
  MapMode = 4
  Placement = pos=(0,0,0) rot=(0.57735,0.57735,0.57735;2.0944rad)
  Support = -> [Sketch]
  sketch-geometry (46):
    g0: BSplineCurve PolesCount=3 KnotsCount=2 Degree=2 IsPeriodic=0
    g1: ArcOfCircle CenterX=73.1223 CenterY=-32.291 CenterZ=0 NormalX=0 NormalY=0 NormalZ=1 AngleXU=0 Radius=13 StartAngle=5.92268 EndAngle=9.06428
    g2: ArcOfCircle CenterX=66.7816 CenterY=-49.1439 CenterZ=0 NormalX=0 NormalY=0 NormalZ=1 AngleXU=0 Radius=13 StartAngle=2.78068 EndAngle=5.92131
    g3: ArcOfCircle CenterX=55.9263 CenterY=-78.1807 CenterZ=0 NormalX=0 NormalY=0 NormalZ=1 AngleXU=0 Radius=13 StartAngle=5.92268 EndAngle=9.06428
    g4: ArcOfCircle CenterX=49.5884 CenterY=-95.0342 CenterZ=0 NormalX=0 NormalY=0 NormalZ=1 AngleXU=0 Radius=13 StartAngle=2.78068 EndAngle=5.92131
    g5: ArcOfCircle CenterX=38.7206 CenterY=-124.067 CenterZ=0 NormalX=0 NormalY=0 NormalZ=1 AngleXU=0 Radius=13 StartAngle=5.92268 EndAngle=9.06428
    g6: ArcOfCircle CenterX=32.3875 CenterY=-140.92 CenterZ=0 NormalX=0 NormalY=0 NormalZ=1 AngleXU=0 Radius=13 StartAngle=2.78068 EndAngle=5.92131
    g7: ArcOfCircle CenterX=21.4715 CenterY=-169.934 CenterZ=0 NormalX=0 NormalY=0 NormalZ=1 AngleXU=0 Radius=13 StartAngle=5.92268 EndAngle=9.06428
    g8: ArcOfCircle CenterX=15.1336 CenterY=-186.787 CenterZ=0 NormalX=0 NormalY=0 NormalZ=1 AngleXU=0 Radius=13 StartAngle=2.78068 EndAngle=5.92131
    g9-g12: Circle x4 (B-spline internal-alignment scaffolding for g13; pole/knot coordinates omitted)
    g13: BSplineCurve PolesCount=4 KnotsCount=2 Degree=3 IsPeriodic=0
    g14: GeomPoint X=28.8094 Y=-19.0875 Z=0
    g15: GeomPoint X=47.0443 Y=-50.4712 Z=0
    g16: Circle CenterX=53.5586 CenterY=-23.2695 CenterZ=0 NormalX=0 NormalY=0 NormalZ=1 AngleXU=0 Radius=3.24518
    g17: Circle CenterX=-195.441 CenterY=-127.082 CenterZ=0 NormalX=0 NormalY=0 NormalZ=1 AngleXU=0 Radius=1
    g18: Circle CenterX=-8.24091 CenterY=-197.481 CenterZ=0 NormalX=0 NormalY=0 NormalZ=1 AngleXU=0 Radius=1
    g19: Circle CenterX=12.8789 CenterY=-141.321 CenterZ=0 NormalX=0 NormalY=0 NormalZ=1 AngleXU=0 Radius=1
    g20: BSplineCurve PolesCount=3 KnotsCount=2 Degree=2 IsPeriodic=0
    g21: GeomPoint X=-195.441 Y=-127.082 Z=0
    g22: GeomPoint X=12.8789 Y=-141.321 Z=0
    g23: Circle CenterX=-12.8016 CenterY=-179.036 CenterZ=0 NormalX=0 NormalY=0 NormalZ=1 AngleXU=0 Radius=10.5072
    g24: Circle CenterX=0.933922 CenterY=-166.43 CenterZ=0 NormalX=0 NormalY=0 NormalZ=1 AngleXU=0 Radius=3.26661
    g25: Circle CenterX=-33.5518 CenterY=-176.44 CenterZ=0 NormalX=0 NormalY=0 NormalZ=1 AngleXU=0 Radius=5.64388
    g26: Circle CenterX=-47.2366 CenterY=-173.859 CenterZ=0 NormalX=0 NormalY=0 NormalZ=1 AngleXU=0 Radius=3.01653
    g27: Circle CenterX=-56.2595 CenterY=-171.456 CenterZ=0 NormalX=0 NormalY=0 NormalZ=1 AngleXU=0 Radius=2.12826
    g28: ArcOfCircle CenterX=51.2151 CenterY=-198.473 CenterZ=0 NormalX=0 NormalY=0 NormalZ=1 AngleXU=0 Radius=20 StartAngle=2.78189 EndAngle=4.35269
    g29: LineSegment StartX=32.4951 StartY=-191.433 StartZ=0 EndX=94.6578 EndY=-26.1352 EndZ=0
    g30: LineSegment StartX=43.1192 StartY=-220.001 StartZ=0 EndX=-196.497 EndY=-129.89 EndZ=0
    g31: LineSegment StartX=43.1192 StartY=-220.001 StartZ=0 EndX=44.1752 EndY=-217.193 EndZ=0
    g32: LineSegment StartX=117.223 StartY=-19.0875 StartZ=0 EndX=117.223 EndY=-16.0875 EndZ=0
    g33: LineSegment StartX=117.223 StartY=-16.0875 StartZ=0 EndX=17.2232 EndY=-16.0875 EndZ=0
    g34: LineSegment StartX=17.2232 StartY=-16.0875 StartZ=0 EndX=17.2232 EndY=-19.0875 EndZ=0
    g35: LineSegment StartX=28.8094 StartY=-19.0875 StartZ=0 EndX=17.2232 EndY=-19.0875 EndZ=0
    g36: LineSegment StartX=47.0443 StartY=-50.4712 StartZ=0 EndX=12.8789 EndY=-141.321 EndZ=0
    g37: LineSegment StartX=-195.441 StartY=-127.082 StartZ=0 EndX=-196.497 EndY=-129.89 EndZ=0
    g38: LineSegment StartX=85.2866 StartY=-36.8766 StartZ=0 EndX=78.9396 EndY=-53.7463 EndZ=0
    g39: LineSegment StartX=60.9579 StartY=-27.7053 StartZ=0 EndX=54.6191 EndY=-44.5532 EndZ=0
    g40: LineSegment StartX=68.0907 StartY=-82.7664 StartZ=0 EndX=61.7465 EndY=-99.6365 EndZ=0
    g41: LineSegment StartX=43.7619 StartY=-73.595 StartZ=0 EndX=37.426 EndY=-90.4435 EndZ=0
    g42: LineSegment StartX=50.885 StartY=-128.652 StartZ=0 EndX=44.5456 EndY=-145.522 EndZ=0
    g43: LineSegment StartX=26.5562 StartY=-119.481 StartZ=0 EndX=20.2251 EndY=-136.329 EndZ=0
    g44: LineSegment StartX=9.3071 StartY=-165.349 StartZ=0 EndX=2.97115 EndY=-182.197 EndZ=0
    g45: LineSegment StartX=33.6358 StartY=-174.52 StartZ=0 EndX=27.2917 EndY=-191.39 EndZ=0
  constraints (71):
    c: Block(g0)
    c: Block(g1)
    c: Block(g2)
    c: Block(g4)
    c: Block(g3)
    c: Block(g6)
    c: Block(g5)
    c: Block(g8)
    c: Block(g7)
    c: Weight(g9) = 1
    c: Equal(g9,g10)
    c: Equal(g9,g11)
    c: Equal(g9,g12)
    c: InternalAlignment(g9-g12 -> g13) x4
    c: InternalAlignment(g14,g13)
    c: InternalAlignment(g15,g13)
    c: Block(g16)
    c: Weight(g17) = 1
    c: Equal(g17,g18)
    c: Equal(g17,g19)
    c: InternalAlignment(g17,g20)
    c: InternalAlignment(g18,g20)
    c: InternalAlignment(g19,g20)
    c: InternalAlignment(g21,g20)
    c: InternalAlignment(g22,g20)
    c: Block(g20)
    c: Block(g23)
    c: Block(g24)
    c: Block(g25)
    c: Block(g26)
    c: Block(g27)
    c: Block(g28)
    c: Coincident(g29,g28)
    c: Coincident(g29,g0)
    c: Block(g13)
    c: Coincident(g31,g30)
    c: Coincident(g31,g28)
    c: Block(g31)
    c: Coincident(g32,g0)
    c: Vertical(g32)
    c: Coincident(g33,g32)
    c: Horizontal(g33)
    c: Coincident(g34,g33)
    c: Vertical(g34)
    c: Block(g33)
    c: Coincident(g35,g13)
    c: Coincident(g35,g34)
    c: Horizontal(g35)
    c: Coincident(g36,g13)
    c: Coincident(g36,g20)
    c: Coincident(g37,g20)
    c: Coincident(g37,g30)
    c: Block(g30)
    c: Coincident(g38,g1)
    c: Coincident(g38,g2)
    c: Coincident(g39,g1)
    c: Coincident(g39,g2)
    c: Coincident(g40,g3)
    c: Coincident(g40,g4)
    c: Coincident(g41,g3)
    c: Coincident(g41,g4)
    c: Coincident(g42,g5)
    c: Coincident(g42,g6)
    c: Coincident(g43,g5)
    c: Coincident(g43,g6)
    c: Coincident(g44,g7)
    c: Coincident(g44,g8)
    c: Coincident(g45,g7)
    c: Coincident(g45,g8)
    c: Distance(g30) = 256
    c: Distance(g33) = 100
FEATURE [Part::Extrusion] Extrude002
  Base = -> Sketch001
  Dir = (1,0,0)
  DirMode = 2
  FaceMakerClass = Part::FaceMakerBullseye
  LengthFwd = 8
  LengthRev = 0
  Solid = true
  Symmetric = false
FEATURE [Sketcher::SketchObject] Sketch002
  FullyConstrained = true
  sketch-geometry (20):
    g0: LineSegment StartX=-2.77179 StartY=-200.304 StartZ=0 EndX=5.22821 EndY=-200.304 EndZ=0
    g1: LineSegment StartX=5.22821 StartY=-200.304 StartZ=0 EndX=5.22821 EndY=-197.304 EndZ=0
    g2: LineSegment StartX=-2.77179 StartY=-200.304 StartZ=0 EndX=-2.77179 EndY=-197.304 EndZ=0
    g3: LineSegment StartX=5.22821 StartY=-197.304 StartZ=0 EndX=8.22821 EndY=-197.304 EndZ=0
    g4: LineSegment StartX=-2.77179 StartY=-197.304 StartZ=0 EndX=-5.77179 EndY=-197.304 EndZ=0
    g5: LineSegment StartX=19.2282 StartY=-203.304 StartZ=0 EndX=19.2282 EndY=-206.304 EndZ=0
    g6: LineSegment StartX=-16.7718 StartY=-203.304 StartZ=0 EndX=-16.7718 EndY=-206.304 EndZ=0
    g7: LineSegment StartX=-16.7718 StartY=-206.304 StartZ=0 EndX=19.2282 EndY=-206.304 EndZ=0
    g8: Circle CenterX=-16.7718 CenterY=-203.304 CenterZ=0 NormalX=0 NormalY=0 NormalZ=1 AngleXU=0 Radius=1
    g9: Circle CenterX=-5.77179 CenterY=-203.304 CenterZ=0 NormalX=0 NormalY=0 NormalZ=1 AngleXU=0 Radius=1
    g10: Circle CenterX=-5.77179 CenterY=-197.304 CenterZ=0 NormalX=0 NormalY=0 NormalZ=1 AngleXU=0 Radius=1
    g11: BSplineCurve PolesCount=3 KnotsCount=2 Degree=2 IsPeriodic=0
    g12: GeomPoint X=-16.7718 Y=-203.304 Z=0
    g13: GeomPoint X=-5.77179 Y=-197.304 Z=0
    g14: Circle CenterX=19.2282 CenterY=-203.304 CenterZ=0 NormalX=0 NormalY=0 NormalZ=1 AngleXU=0 Radius=1
    g15: Circle CenterX=8.22821 CenterY=-203.304 CenterZ=0 NormalX=0 NormalY=0 NormalZ=1 AngleXU=0 Radius=1
    g16: Circle CenterX=8.22821 CenterY=-197.304 CenterZ=0 NormalX=0 NormalY=0 NormalZ=1 AngleXU=0 Radius=1
    g17: BSplineCurve PolesCount=3 KnotsCount=2 Degree=2 IsPeriodic=0
    g18: GeomPoint X=19.2282 Y=-203.304 Z=0
    g19: GeomPoint X=8.22821 Y=-197.304 Z=0
  constraints (41):
    c: Horizontal(g0)
    c: Distance(g0) = 8
    c: Coincident(g1,g0)
    c: Vertical(g1)
    c: Distance(g1) = 3
    c: Coincident(g2,g0)
    c: Vertical(g2)
    c: Distance(g2) = 3
    c: Coincident(g3,g1)
    c: Horizontal(g3)
    c: Distance(g3) = 3
    c: Coincident(g4,g2)
    c: Horizontal(g4)
    c: Distance(g4) = 3
    c: Vertical(g5)
    c: Vertical(g6)
    c: Coincident(g7,g6)
    c: Coincident(g7,g5)
    c: Weight(g8) = 1
    c: Equal(g8,g9)
    c: Equal(g8,g10)
    c: Coincident(g11,g4)
    c: InternalAlignment(g8,g11)
    c: InternalAlignment(g9,g11)
    c: InternalAlignment(g10,g11)
    c: InternalAlignment(g12,g11)
    c: InternalAlignment(g13,g11)
    c: Coincident(g17,g5)
    c: Weight(g14) = 1
    c: Equal(g14,g15)
    c: Equal(g14,g16)
    c: Coincident(g17,g3)
    c: InternalAlignment(g14,g17)
    c: InternalAlignment(g15,g17)
    c: InternalAlignment(g16,g17)
    c: InternalAlignment(g18,g17)
    c: InternalAlignment(g19,g17)
    c: Block(g7)
    c: Block(g17)
    c: Block(g11)
    c: Block(g6)
FEATURE [Part::Extrusion] Extrude003
  Base = -> Sketch002
  Dir = (0,0,1)
  DirMode = 2
  FaceMakerClass = Part::FaceMakerBullseye
  LengthFwd = 260
  LengthRev = 0
  Solid = true
  Symmetric = false
FEATURE [Part::Extrusion] Extrude
  Base = -> Sketch
  Dir = (0,0,1)
  DirMode = 2
  FaceMakerClass = Part::FaceMakerBullseye
  LengthFwd = 14
  LengthRev = 0
  Solid = true
  Symmetric = false
